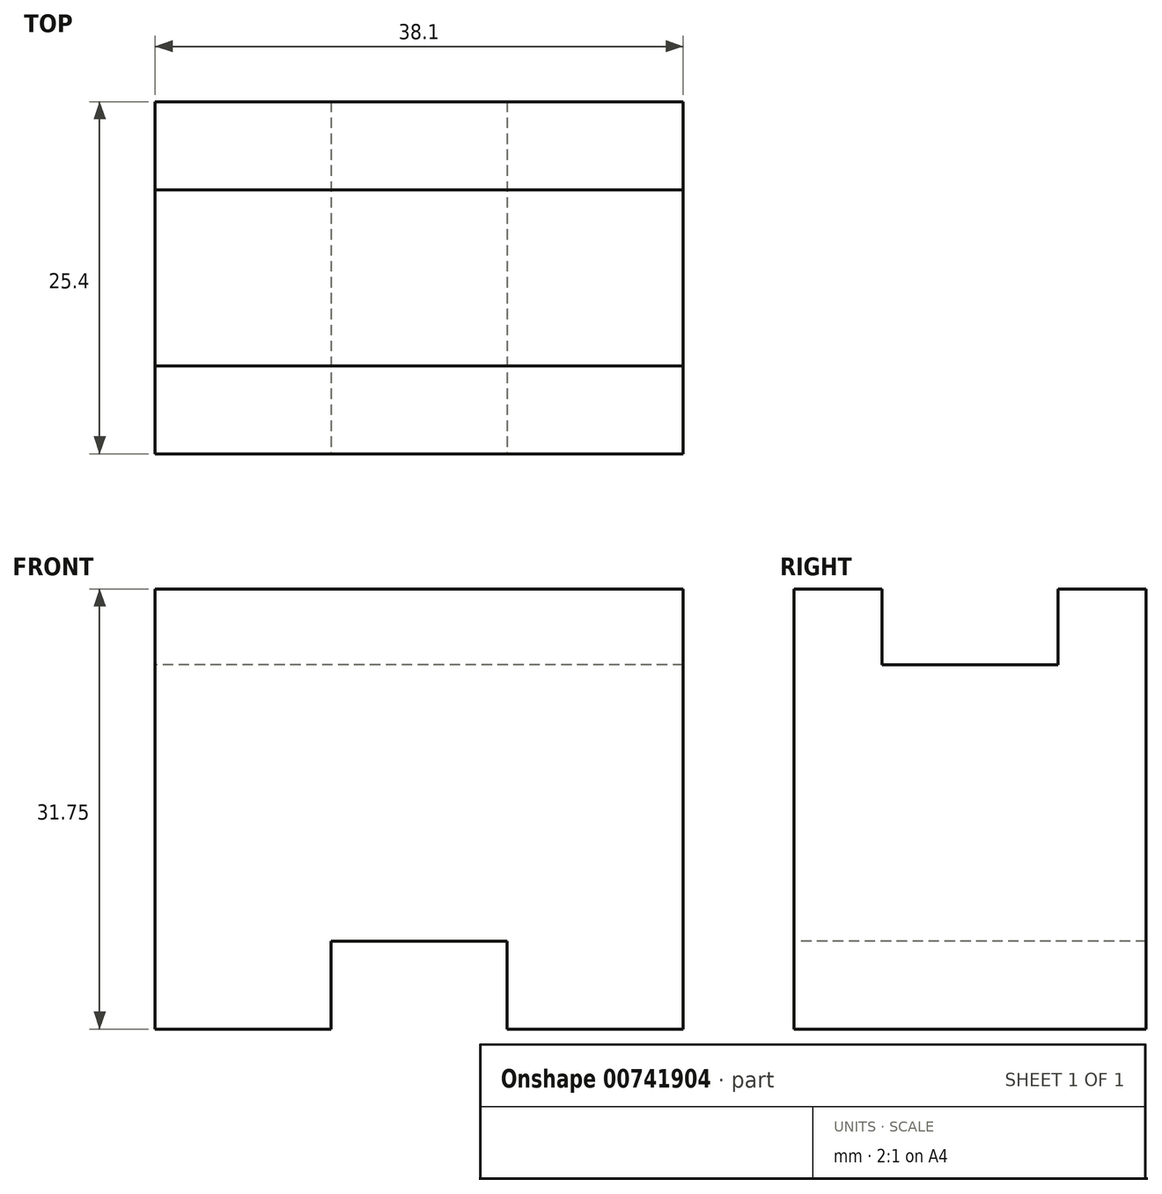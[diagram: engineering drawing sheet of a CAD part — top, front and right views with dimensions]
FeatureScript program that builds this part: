
annotation { "Feature Type Name" : "Feature", "Feature Type Description" : "" }
export const myFeature = defineFeature(function(context is Context, id is Id, definition is map)
    precondition{}
    {
        {
            var Q0;
            Q0=qCreatedBy(makeId("Right.planeOp"),FACE);
            var sketch = newSketch(context, id + "F0", { "sketchPlane" : qUnion([Q0])});
            skLineSegment(sketch, "E0", {"start": v(0, 31.75) * mm, "end": v(6.35, 31.75) * mm});
            skLineSegment(sketch, "E1", {"start": v(6.35, 32) * mm, "end": v(6.35, 26.27) * mm});
            skLineSegment(sketch, "E2", {"start": v(6.35, 26.27) * mm, "end": v(19.05, 26.27) * mm});
            skLineSegment(sketch, "E3", {"start": v(19.05, 26.27) * mm, "end": v(19.05, 31.75) * mm});
            skLineSegment(sketch, "E4", {"start": v(19.05, 31.75) * mm, "end": v(25.4, 31.75) * mm});
            skLineSegment(sketch, "E5", {"start": v(25.4, 31.75) * mm, "end": v(25.4, 0) * mm});
            skLineSegment(sketch, "E6", {"start": v(25.4, 0) * mm, "end": v(0, 0) * mm});
            skLineSegment(sketch, "E7", {"start": v(0, 0) * mm, "end": v(0, 31.75) * mm});
            skSolve(sketch);
        }
        {
            var Q0;
            {var subQ2=sQuery(id+"F0.wireOp",EDGE,"E0");Q0=makeQuery(id+"F0.imprint","IMPRINT",FACE,{"disambiguationData":[TD([[makeQuery(id+"F0.imprint","IMPRINT",EDGE,{"derivedFrom":subQ2}),-1.0]])]});}
            extrude(context, id + "F1", {"entities" : qUnion([Q0]), "depth" : 38.1 * mm, "offsetDistance" : 25.4 * mm});
        }
        {
            var Q0;
            Q0=makeQuery(id+"F1.opExtrude","SWEPT_FACE",FACE,{"disambiguationData":[OSD([sQuery(id+"F0.wireOp",EDGE,"E7")])]});
            var sketch = newSketch(context, id + "F2", { "sketchPlane" : qUnion([Q0])});
            skLineSegment(sketch, "E8", {"start": v(12.7, 0) * mm, "end": v(12.7, 6.35) * mm});
            skLineSegment(sketch, "E9", {"start": v(12.7, 6.35) * mm, "end": v(25.4, 6.35) * mm});
            skLineSegment(sketch, "E10", {"start": v(25.4, 6.35) * mm, "end": v(25.4, 0) * mm});
            skLineSegment(sketch, "E11", {"start": v(25.4, 0) * mm, "end": v(38.1, 0) * mm});
            skSolve(sketch);
        }
        {
            var Q0;
            {var subQ0=sQuery(id+"F2.wireOp",EDGE,"E8");Q0=makeQuery(id+"F2.imprint","IMPRINT",FACE,{"disambiguationData":[TD([[makeQuery(id+"F2.imprint","IMPRINT",EDGE,{"derivedFrom":subQ0}),-1.0]])]});}
            extrude(context, id + "F3", {"entities" : qUnion([Q0]), "operationType" : NewBodyOperationType.REMOVE, "endBound" : BoundingType.THROUGH_ALL, "oppositeDirection" : true, "depth" : 25.4 * mm, "offsetDistance" : 25.4 * mm});
        }
    });
